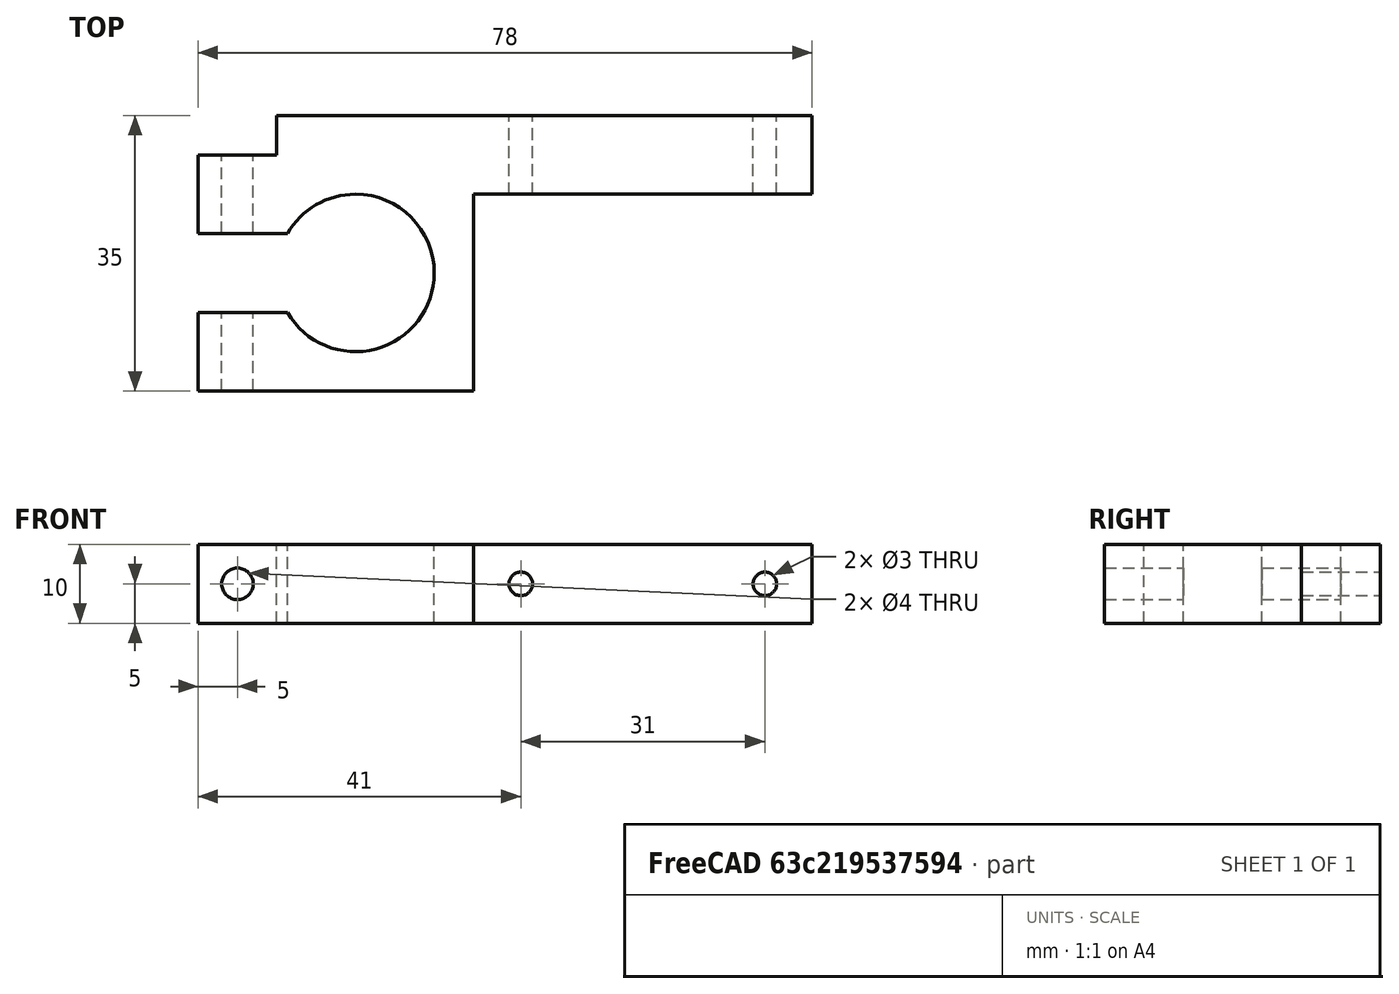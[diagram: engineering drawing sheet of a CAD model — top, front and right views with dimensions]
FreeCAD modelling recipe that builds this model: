
FCSTD DOCUMENT  (FreeCAD 0.17R13522 (Git))
Label: fastener-nema-17
License: All rights reserved
LicenseURL: http://en.wikipedia.org/wiki/All_rights_reserved
objects: Part::Cylinder×4, Part::Box×3, Part::MultiFuse×2, Part::Cut×1
note: 10 computed .brp shape members not serialized (recipe doc carries the construction recipe); baked Part::Feature solids carry a one-line shape summary decoded from their .brp

FEATURE [Part::Box] Box  label="Cube"
  AttacherType = Attacher::AttachEngine3D
  Height = 10
  Length = 35
  Placement = pos=(-20,-15,-5) rot=(0,0,1;0rad)
  Width = 30
FEATURE [Part::Cylinder] Cylinder
  Angle = 360
  AttacherType = Attacher::AttachEngine3D
  Height = 10
  Placement = pos=(0,0,-5) rot=(0,0,1;0rad)
  Radius = 10
FEATURE [Part::Box] Box001  label="Cube001"
  AttacherType = Attacher::AttachEngine3D
  Height = 10
  Length = 15
  Placement = pos=(-20,-5,-5) rot=(0,0,1;0rad)
  Width = 10
FEATURE [Part::Cylinder] Cylinder001
  Angle = 360
  AttacherType = Attacher::AttachEngine3D
  Height = 30
  Placement = pos=(-15,-15,0) rot=(-1,0,0;1.5708rad)
  Radius = 2
FEATURE [Part::Box] Box002  label="Cube002"
  AttacherType = Attacher::AttachEngine3D
  Height = 10
  Length = 68
  Placement = pos=(-10,10,-5) rot=(0,0,1;0rad)
  Width = 10
FEATURE [Part::Cylinder] Cylinder002
  Angle = 360
  AttacherType = Attacher::AttachEngine3D
  Height = 10
  Placement = pos=(21,10,0) rot=(-1,0,0;1.5708rad)
  Radius = 1.5
FEATURE [Part::Cylinder] Cylinder003
  Angle = 360
  AttacherType = Attacher::AttachEngine3D
  Height = 10
  Placement = pos=(52,10,0) rot=(-1,0,0;1.5708rad)
  Radius = 1.5
FEATURE [Part::MultiFuse] Fusion  label="Negative Fusion"
  Shapes = -> [Box001,Cylinder,Cylinder001,Cylinder003,Cylinder002]
FEATURE [Part::MultiFuse] Fusion001  label="Positive Fusion"
  Shapes = -> [Box002,Box]
FEATURE [Part::Cut] Cut
  Base = -> Fusion001
  Tool = -> Fusion
